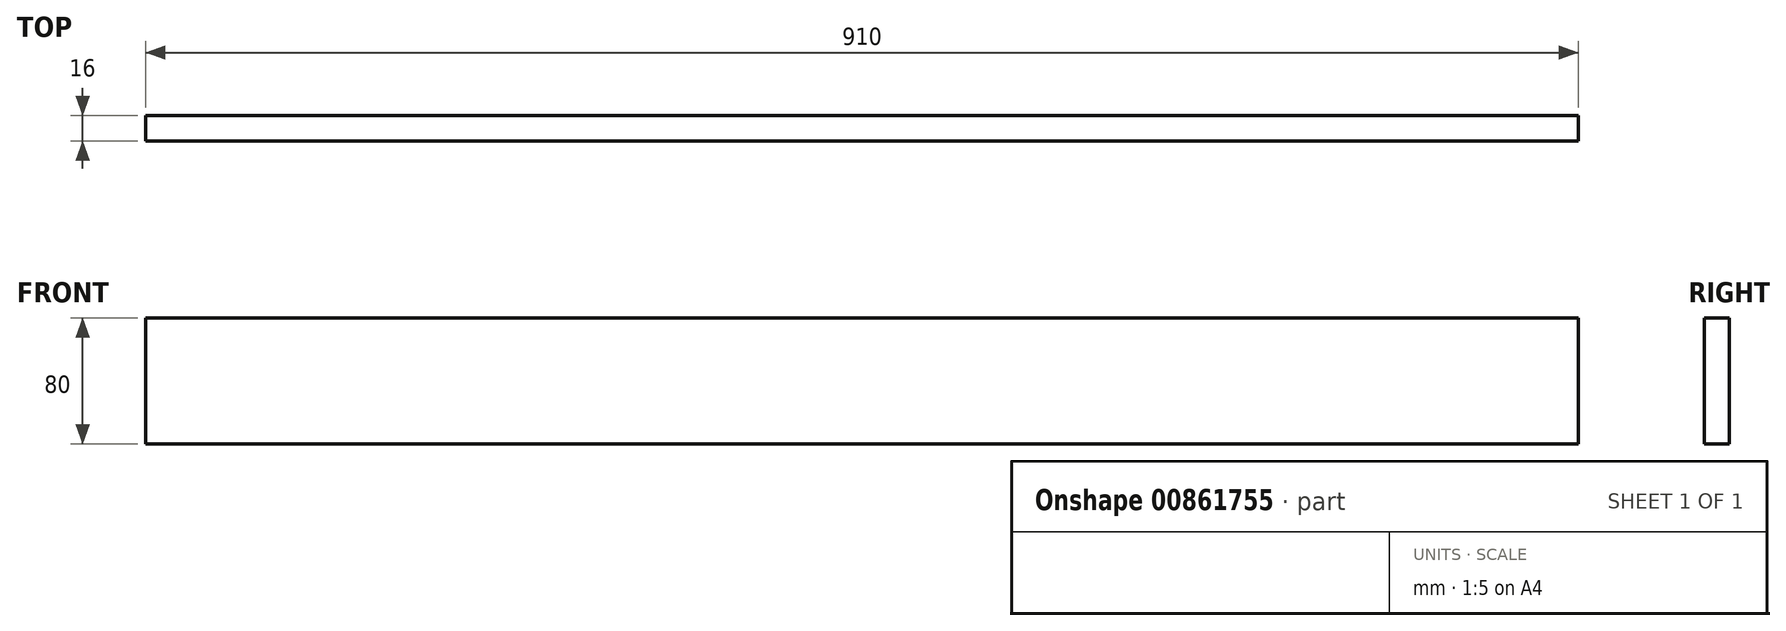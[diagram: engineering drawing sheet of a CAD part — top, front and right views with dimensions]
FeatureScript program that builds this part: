
annotation { "Feature Type Name" : "Feature", "Feature Type Description" : "" }
export const myFeature = defineFeature(function(context is Context, id is Id, definition is map)
    precondition{}
    {
        {
            var Q0;
            Q0=qCreatedBy(makeId("Front.planeOp"),FACE);
            var sketch = newSketch(context, id + "F0", { "sketchPlane" : qUnion([Q0])});
            skLineSegment(sketch, "E0.bottom", {"start": v(-192.83, 45.58) * mm, "end": v(717.17, 45.58) * mm});
            skLineSegment(sketch, "E0.top", {"start": v(-192.83, -34.42) * mm, "end": v(717.17, -34.42) * mm});
            skLineSegment(sketch, "E0.left", {"start": v(-192.83, 45.58) * mm, "end": v(-192.83, -34.42) * mm});
            skLineSegment(sketch, "E0.right", {"start": v(717.17, 45.58) * mm, "end": v(717.17, -34.42) * mm});
            skSolve(sketch);
        }
        {
            var Q0;
            Q0=makeQuery(id+"F0.imprint","IMPRINT",FACE,{"disambiguationData":[TD([[makeQuery(id+"F0.imprint","IMPRINT",EDGE,{"derivedFrom":sQuery(id+"F0.wireOp",EDGE,"E0.bottom")}),-1.0]])]});
            extrude(context, id + "F1", {"entities" : qUnion([Q0]), "depth" : 16 * mm, "offsetDistance" : 25 * mm});
        }
    });
